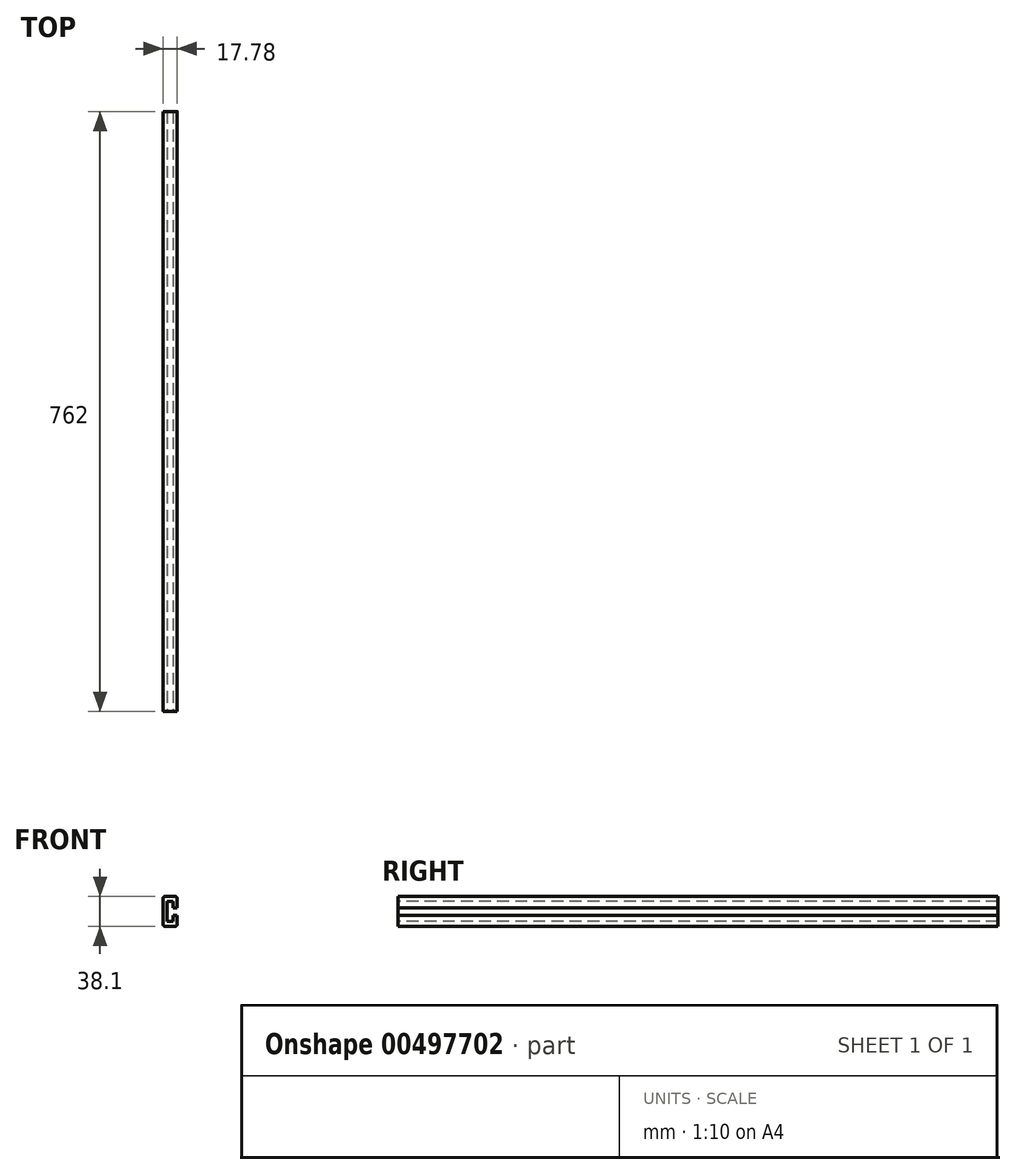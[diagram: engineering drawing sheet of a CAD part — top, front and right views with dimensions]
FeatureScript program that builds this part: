
annotation { "Feature Type Name" : "Feature", "Feature Type Description" : "" }
export const myFeature = defineFeature(function(context is Context, id is Id, definition is map)
    precondition{}
    {
        {
            var Q0;
            Q0=qCreatedBy(makeId("Top.planeOp"),FACE);
            var sketch = newSketch(context, id + "F0", { "sketchPlane" : qUnion([Q0])});
            skLineSegment(sketch, "E0", {"start": v(-1554.23, 762) * mm, "end": v(-1554.23, 0) * mm});
            skLineSegment(sketch, "E1", {"start": v(-1554.23, 762) * mm, "end": v(-1566.93, 762) * mm});
            skLineSegment(sketch, "E2", {"start": v(-1566.93, 762) * mm, "end": v(-1554.23, 762) * mm});
            skLineSegment(sketch, "E3", {"start": v(-1554.23, 0) * mm, "end": v(-1566.93, 0) * mm});
            skLineSegment(sketch, "E4", {"start": v(-1566.93, 762) * mm, "end": v(-1566.93, 0) * mm});
            skSolve(sketch);
        }
        {
            var Q0;
            Q0=makeQuery(id+"F0.imprint","IMPRINT",FACE,{"disambiguationData":[TD([[makeQuery(id+"F0.imprint","IMPRINT",EDGE,{"derivedFrom":sQuery(id+"F0.wireOp",EDGE,"E0")}),-1.0]])]});
            extrude(context, id + "F1", {"entities" : qUnion([Q0]), "depth" : 38.1 * mm, "offsetDistance" : 25.4 * mm});
        }
        {
            var Q0;
            Q0=makeQuery(id+"F1.opExtrude","SWEPT_FACE",FACE,{"disambiguationData":[OSD([sQuery(id+"F0.wireOp",EDGE,"E3")])]});
            var sketch = newSketch(context, id + "F2", { "sketchPlane" : qUnion([Q0])});
            skSolve(sketch);
        }
        {
            var Q0;
            Q0=makeQuery(id+"F1.opExtrude","SWEPT_FACE",FACE,{"disambiguationData":[OSD([sQuery(id+"F0.wireOp",EDGE,"E0")])]});
            var sketch = newSketch(context, id + "F3", { "sketchPlane" : qUnion([Q0])});
            skLineSegment(sketch, "E5", {"start": v(381, 14.29) * mm, "end": v(0, 14.29) * mm});
            skLineSegment(sketch, "E6", {"start": v(381, 23.81) * mm, "end": v(0, 23.81) * mm});
            skLineSegment(sketch, "E7", {"start": v(381, 14.29) * mm, "end": v(762, 14.29) * mm});
            skLineSegment(sketch, "E8", {"start": v(381, 23.81) * mm, "end": v(762, 23.81) * mm});
            skSolve(sketch);
        }
        {
            var Q0;
            {var subQ3=sQuery(id+"F3.wireOp",EDGE,"E5");Q0=makeQuery(id+"F3.imprint","IMPRINT",FACE,{"disambiguationData":[TD([[makeQuery(id+"F3.imprint","IMPRINT",EDGE,{"derivedFrom":subQ3}),-1.0]])]});}
            extrude(context, id + "F4", {"entities" : qUnion([Q0]), "operationType" : NewBodyOperationType.REMOVE, "oppositeDirection" : true, "depth" : 5.08 * mm, "offsetDistance" : 25.4 * mm});
        }
        {
            var Q0;
            Q0=makeQuery(id+"F1.opExtrude","SWEPT_FACE",FACE,{"disambiguationData":[OSD([sQuery(id+"F0.wireOp",EDGE,"E4")])]});
            extrude(context, id + "F5", {"entities" : qUnion([Q0]), "operationType" : NewBodyOperationType.ADD, "depth" : 5.08 * mm, "offsetDistance" : 25.4 * mm});
        }
        {
            var Q0;
            {var subQ0=sQuery(id+"F0.wireOp",EDGE,"E3");Q0=makeQuery(id+"F5.boolean.opBoolean","MERGE",FACE,{"derivedFrom":[makeQuery(id+"F1.opExtrude","SWEPT_FACE",FACE,{"disambiguationData":[OSD([subQ0])]}),makeQuery(id+"F5.opExtrude","SWEPT_FACE",FACE,{"disambiguationData":[OSD([subQ0,sQuery(id+"F0.wireOp",EDGE,"E4")])]})]});}
            var sketch = newSketch(context, id + "F6", { "sketchPlane" : qUnion([Q0])});
            skLineSegment(sketch, "E9", {"start": v(-1566.93, 31.75) * mm, "end": v(-1566.93, 6.35) * mm});
            skLineSegment(sketch, "E10", {"start": v(-1566.93, 6.35) * mm, "end": v(-1559.3, 6.35) * mm});
            skLineSegment(sketch, "E11", {"start": v(-1566.93, 31.75) * mm, "end": v(-1559.3, 31.75) * mm});
            skLineSegment(sketch, "E12", {"start": v(-1559.3, 31.75) * mm, "end": v(-1559.3, 6.35) * mm});
            skSolve(sketch);
        }
        {
            var Q0;
            Q0=makeQuery(id+"F6.imprint","IMPRINT",FACE,{"disambiguationData":[TD([[makeQuery(id+"F6.imprint","IMPRINT",EDGE,{"derivedFrom":sQuery(id+"F6.wireOp",EDGE,"E9")}),1.0]])]});
            extrude(context, id + "F7", {"entities" : qUnion([Q0]), "operationType" : NewBodyOperationType.REMOVE, "oppositeDirection" : true, "depth" : 762 * mm, "offsetDistance" : 25.4 * mm});
        }
        {
            var Q0;
            {var subQ0=sQuery(id+"F0.wireOp",EDGE,"E4");Q0=makeQuery(id+"F5.opExtrude","CAP_EDGE",EDGE,{"disambiguationData":[OSD([subQ0]),TDD([makeQuery(id+"F1.opExtrude","CAP_EDGE",EDGE,{"disambiguationData":[OSD([subQ0])],"isStart":false})])],"isStart":false});}
            fillet(context, id + "F8", {"entities" : qUnion([Q0]), "radius" : 2.54 * mm, "tangentPropagation" : true, "allowEdgeOverflow" : false});
        }
        {
            var Q0;
            Q0=makeQuery(id+"F1.opExtrude","CAP_EDGE",EDGE,{"disambiguationData":[OSD([sQuery(id+"F0.wireOp",EDGE,"E0")])],"isStart":true});
            fillet(context, id + "F9", {"entities" : qUnion([Q0]), "radius" : 2.54 * mm, "tangentPropagation" : true, "allowEdgeOverflow" : false});
        }
        {
            var Q0;
            {var subQ0=sQuery(id+"F0.wireOp",EDGE,"E4");Q0=makeQuery(id+"F5.opExtrude","CAP_EDGE",EDGE,{"disambiguationData":[OSD([subQ0]),TDD([makeQuery(id+"F1.opExtrude","CAP_EDGE",EDGE,{"disambiguationData":[OSD([subQ0])],"isStart":true})])],"isStart":false});}
            fillet(context, id + "F10", {"entities" : qUnion([Q0]), "radius" : 2.54 * mm, "tangentPropagation" : true, "allowEdgeOverflow" : false});
        }
        {
            var Q0;
            Q0=makeQuery(id+"F1.opExtrude","CAP_EDGE",EDGE,{"disambiguationData":[OSD([sQuery(id+"F0.wireOp",EDGE,"E0")])],"isStart":false});
            fillet(context, id + "F11", {"entities" : qUnion([Q0]), "radius" : 2.54 * mm, "tangentPropagation" : true, "allowEdgeOverflow" : false});
        }
    });
